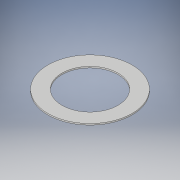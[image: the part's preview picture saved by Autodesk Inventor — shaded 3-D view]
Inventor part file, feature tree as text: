
AUTODESK INVENTOR PART (.ipt)
format: ipt  version: 2019 (Build 230136000, 136)  size: 99,840 bytes
history: native  units: mm
features: other x1, extrude x1, sketch x1
ambient origin geometry x8: Origin, YZ Plane, XZ Plane, XY Plane, X Axis, Y Axis, Z Axis, Center Point
bodies: Body1 (feature_tree)
feature tree (3):
  other  "Sólido1"
  extrude  "Extrusión1"  Depth=0.1mm
  sketch  "Boceto1"  dims[d0=4.0mm d1=6.0mm d2=0.1mm d3=0.0mm]
